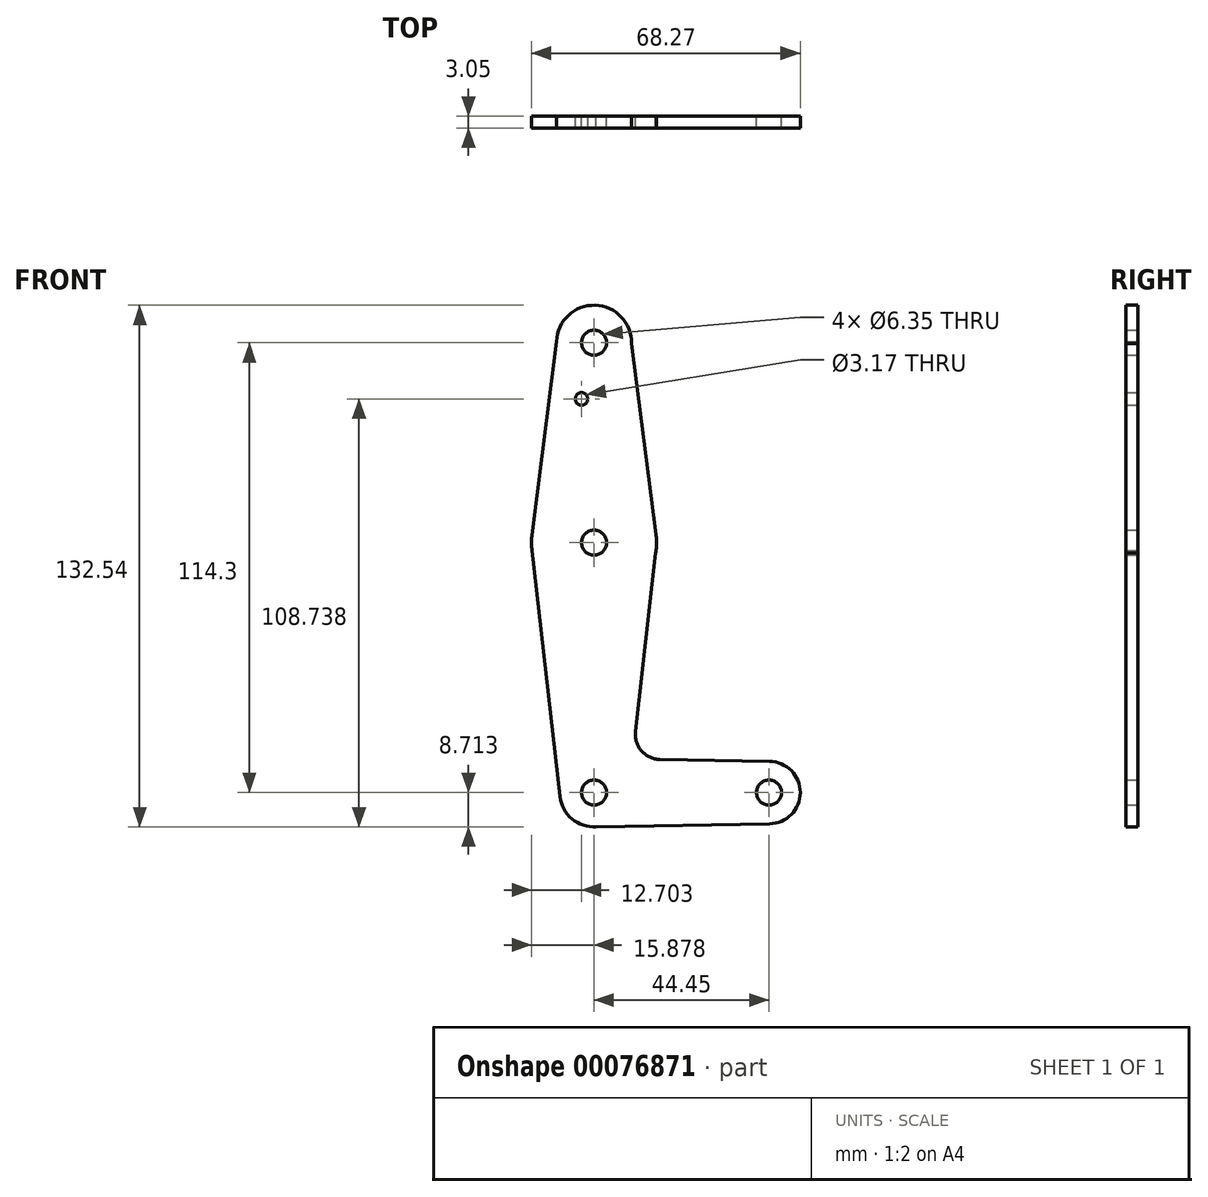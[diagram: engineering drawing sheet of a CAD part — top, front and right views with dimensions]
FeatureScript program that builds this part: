
annotation { "Feature Type Name" : "Feature", "Feature Type Description" : "" }
export const myFeature = defineFeature(function(context is Context, id is Id, definition is map)
    precondition{}
    {
        {
            var Q0;
            Q0=qCreatedBy(makeId("Front.planeOp"),FACE);
            var sketch = newSketch(context, id + "F0", { "sketchPlane" : qUnion([Q0])});
            skCircle(sketch, "E0", {"center": v(-102.94, 425.6) * mm, "radius": 9.53 * mm});
            skCircle(sketch, "E1", {"center": v(-102.94, 374.8) * mm, "radius": 15.88 * mm});
            skCircle(sketch, "E2", {"center": v(-102.94, 311.3) * mm, "radius": 8.72 * mm});
            skCircle(sketch, "E3", {"center": v(-58.5, 311.3) * mm, "radius": 7.94 * mm});
            skLineSegment(sketch, "E4", {"start": v(-102.94, 425.6) * mm, "end": v(-102.94, 374.8) * mm});
            skLineSegment(sketch, "E5", {"start": v(-102.94, 374.8) * mm, "end": v(-102.94, 311.3) * mm});
            skLineSegment(sketch, "E6", {"start": v(-102.94, 311.3) * mm, "end": v(-58.5, 311.3) * mm});
            skLineSegment(sketch, "E7", {"start": v(-112.46, 425.92) * mm, "end": v(-118.7, 376.8) * mm});
            skLineSegment(sketch, "E8", {"start": v(-118.7, 372.8) * mm, "end": v(-111.6, 310.32) * mm});
            skLineSegment(sketch, "E9", {"start": v(-93.42, 425.39) * mm, "end": v(-87.2, 376.82) * mm});
            skLineSegment(sketch, "E10", {"start": v(-87.3, 372.14) * mm, "end": v(-92.42, 326.79) * mm});
            skLineSegment(sketch, "E11", {"start": v(-86.22, 319.73) * mm, "end": v(-58.35, 319.24) * mm});
            skLineSegment(sketch, "E12", {"start": v(-103.2, 302.6) * mm, "end": v(-58.35, 303.37) * mm});
            skCircle(sketch, "E13", {"center": v(-102.94, 425.6) * mm, "radius": 3.18 * mm});
            skCircle(sketch, "E14", {"center": v(-102.94, 374.8) * mm, "radius": 3.18 * mm});
            skCircle(sketch, "E15", {"center": v(-102.94, 311.3) * mm, "radius": 3.18 * mm});
            skCircle(sketch, "E16", {"center": v(-58.5, 311.3) * mm, "radius": 3.18 * mm});
            skCircle(sketch, "E17", {"center": v(-106.12, 411.33) * mm, "radius": 1.59 * mm});
            skArc(sketch, "E18.filletArc", {"start": v(-92.42, 326.79) * mm, "mid": v(-90.88, 321.89) * mm, "end": v(-86.22, 319.73) * mm});
            skSolve(sketch);
        }
        {
            var Q0;
            Q0 = qSketchRegion(id + "F0", true);
            var Q1;
            {var subQ0=sQuery(id+"F0.wireOp",EDGE,"E5");var subQ1=sQuery(id+"F0.wireOp",EDGE,"E2");var subQ2=makeQuery(id+"F0.imprint","INTERSECT",VERTEX,{"derivedFrom":[subQ1,subQ0]});Q1=makeQuery(id+"F0.imprint","IMPRINT",FACE,{"disambiguationData":[TD([[makeQuery(id+"F0.imprint","IMPRINT",EDGE,{"disambiguationData":[TD([[subQ2,1.0]])],"derivedFrom":subQ1}),1.0]])]});}
            extrude(context, id + "F1", {"entities" : qUnion([Q0, Q1]), "depth" : 3.05 * mm});
        }
    });
